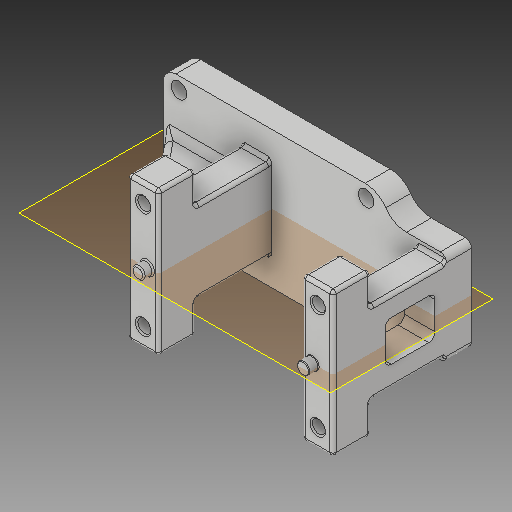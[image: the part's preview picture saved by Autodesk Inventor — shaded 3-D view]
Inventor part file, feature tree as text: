
AUTODESK INVENTOR PART (.ipt)
format: ipt  version: 2019 (Build 230136000, 136)  size: 432,640 bytes
history: native  units: mm
features: fillet x12, extrude x10, sketch x10, chamfer x1, pattern_linear x1, plane x1
ambient origin geometry x8: Origin, YZ Plane, XZ Plane, XY Plane, X Axis, Y Axis, Z Axis, Center Point
bodies: Solid1 (feature_tree)
feature tree (35):
  extrude  "Extrusion1"  Depth=18.0mm
  extrude  "Extrusion2"  Depth=22.0mm
  extrude  "Extrusion3"  Depth=2.5mm
  fillet  "Fillet1"  Radius=2.5mm
  fillet  "Fillet2"  Radius=2.5mm
  extrude  "Extrusion4"  Depth=10.0mm
  extrude  "Extrusion5"  Depth=4.9mm
  extrude  "Extrusion6"  Depth=0.9mm
  chamfer  "Chamfer1"  Distance=1.5mm
  fillet  "Fillet3"  Radius=0.2mm
  fillet  "Fillet4"  Radius=0.2mm
  pattern_linear  "Rectangular Pattern1"  Spacing1=6.0mm  [1 undecoded]
  extrude  "Extrusion7"  Depth=1.0mm TaperAngle=0.0deg
  fillet  "Fillet5"  Radius=17.0mm
  fillet  "Fillet6"  Radius=2.1mm
  extrude  "Extrusion8"  Depth=1.0mm
  fillet  "Fillet7"  Radius=10.0mm
  fillet  "Fillet8"  Radius=2.0mm
  plane  "Work Plane1"
  extrude  "Extrusion9"  Depth=1.0mm
  fillet  "Fillet9"  Radius=0.5mm
  fillet  "Fillet10"  Radius=20.0mm
  fillet  "Fillet11"  Radius=2.0mm
  extrude  "Extrusion10"  Depth=1.0mm
  fillet  "Fillet12"  Radius=2.299822mm
  sketch  "Sketch1"  dims[d0=30.0mm d1=18.0mm]
  sketch  "Sketch2"  dims[d2=35.0mm d3=22.0mm]
  sketch  "Sketch3"  dims[d4=2.5mm d5=2.5mm d6=2.5mm d7=2.5mm]
  sketch  "Sketch5"  dims[d8=4.0mm d9=0.0mm d10=10.0mm]
  sketch  "Sketch6"  dims[d11=13.0mm d12=4.9mm]
  sketch  "Sketch7"  dims[d13=18.2mm d14=0.0mm d15=0.9mm]
  sketch  "Sketch8"  dims[d16=2.0mm]
  sketch  "Sketch10"  dims[d17=1.95mm d18=1.5mm d19=0.0mm d20=0.2mm d21=0.2mm]
  sketch  "Sketch12"  dims[d23=6.0mm]
  sketch  "Sketch14"  dims[d24=5.0mm d25=0.0mm d26=6.0mm d27=5.0mm d28=0.0mm d29=17.0mm d30=2.1mm d31=2.1mm d32=10.0mm d33=0.0mm d34=0.2mm d35=2.0mm d36=45.0deg d37=0.5mm d38=0.5mm d39=20.0mm d41=28.0mm d43=2.0mm d44=1.95mm d45=2.299822mm d46=1.5mm d47=0.0mm d48=0.1mm d49=0.1mm d50=15.0mm d51=4.0mm d52=10.4mm d53=0.0mm d54=4.0mm d55=1.0mm d56=15.0mm d57=12.0mm d58=5.0mm d59=0.0mm d60=1.0mm d61=0.5mm d62=2.0mm d63=8.0mm d64=6.5mm d65=5.0mm d66=0.0mm d67=1.0mm]
note: 1 required parameter value undecoded (feature->parameter linkage not recoverable at this tier; creation-order binding heuristic only, values carry confidence <= 0.55)
